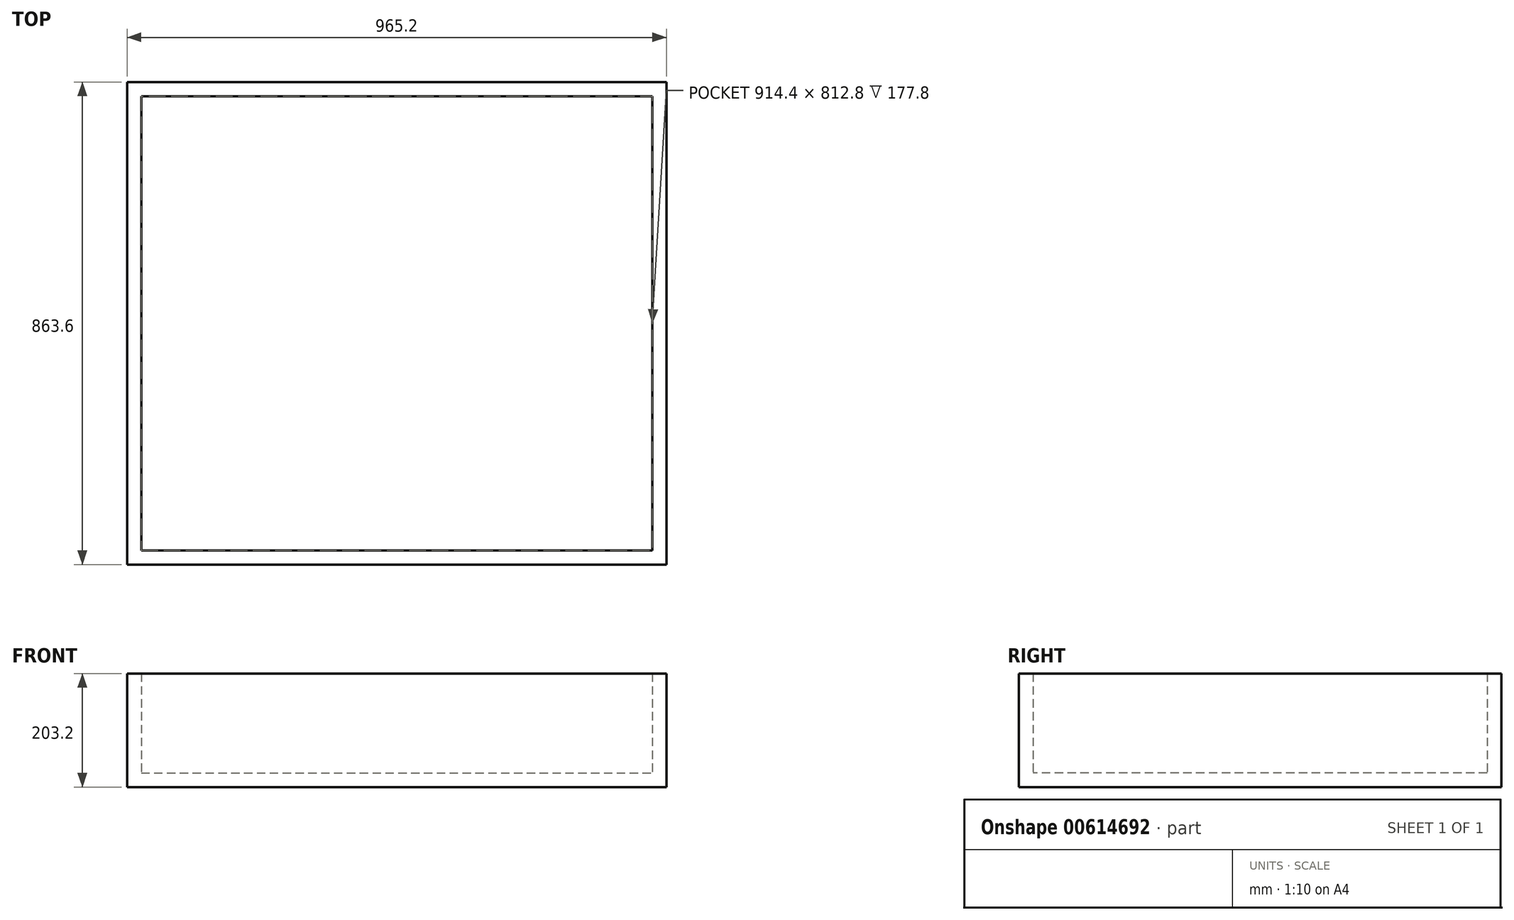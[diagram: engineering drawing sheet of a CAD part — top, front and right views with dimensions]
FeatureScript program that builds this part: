
annotation { "Feature Type Name" : "Feature", "Feature Type Description" : "" }
export const myFeature = defineFeature(function(context is Context, id is Id, definition is map)
    precondition{}
    {
        {
            var Q0;
            Q0=qCreatedBy(makeId("Top.planeOp"),FACE);
            var sketch = newSketch(context, id + "F0", { "sketchPlane" : qUnion([Q0])});
            skLineSegment(sketch, "E0.bottom", {"start": v(-452.65, 460.71) * mm, "end": v(461.75, 460.71) * mm});
            skLineSegment(sketch, "E0.top", {"start": v(-452.65, -352.09) * mm, "end": v(461.75, -352.09) * mm});
            skLineSegment(sketch, "E0.left", {"start": v(-452.65, 460.71) * mm, "end": v(-452.65, -352.09) * mm});
            skLineSegment(sketch, "E0.right", {"start": v(461.75, 460.71) * mm, "end": v(461.75, -352.09) * mm});
            skLineSegment(sketch, "E1.0", {"start": v(-478.05, 486.11) * mm, "end": v(487.15, 486.11) * mm});
            skLineSegment(sketch, "E1.1", {"start": v(-478.05, 486.11) * mm, "end": v(-478.05, -377.49) * mm});
            skLineSegment(sketch, "E1.2", {"start": v(-478.05, -377.49) * mm, "end": v(487.15, -377.49) * mm});
            skLineSegment(sketch, "E1.3", {"start": v(487.15, 486.11) * mm, "end": v(487.15, -377.49) * mm});
            skSolve(sketch);
        }
        {
            var Q0;
            Q0=makeQuery(id+"F0.imprint","IMPRINT",FACE,{"disambiguationData":[TD([[makeQuery(id+"F0.imprint","IMPRINT",EDGE,{"derivedFrom":sQuery(id+"F0.wireOp",EDGE,"E0.bottom")}),-1.0]])]});
            extrude(context, id + "F1", {"entities" : qUnion([Q0]), "depth" : 25.4 * mm, "offsetDistance" : 25.4 * mm});
        }
        {
            var Q0;
            Q0=makeQuery(id+"F0.imprint","IMPRINT",FACE,{"disambiguationData":[TD([[makeQuery(id+"F0.imprint","IMPRINT",EDGE,{"derivedFrom":sQuery(id+"F0.wireOp",EDGE,"E0.bottom")}),1.0]])]});
            extrude(context, id + "F2", {"entities" : qUnion([Q0]), "operationType" : NewBodyOperationType.ADD, "depth" : 203.2 * mm, "offsetDistance" : 25.4 * mm});
        }
    });
